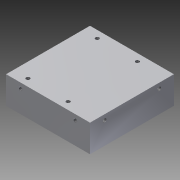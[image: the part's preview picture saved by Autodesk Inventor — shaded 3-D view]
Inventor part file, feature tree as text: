
AUTODESK INVENTOR PART (.ipt)
format: ipt  version: 2013 (Build 170138000, 138)  size: 140,288 bytes
history: native  units: mm
features: thread x12, sketch x4, hole x3, other x1, extrude x1
ambient origin geometry x1: Origin
feature tree (21):
  other  "ソリッド1"
  extrude  "押し出し1"  Depth=46.0mm
  hole  "穴1"  [1 undecoded]
  hole  "穴2"  [1 undecoded]
  hole  "穴3"  [1 undecoded]
  thread  "ねじ1"
  thread  "ねじ3"
  thread  "ねじ5"
  thread  "ねじ6"
  thread  "ねじ11"
  thread  "ねじ13"
  thread  "ねじ14"
  thread  "ねじ16"
  thread  "ねじ17"
  thread  "ねじ18"
  thread  "ねじ19"
  thread  "ねじ20"
  sketch  "スケッチ1"
  sketch  "スケッチ2"
  sketch  "スケッチ3"
  sketch  "スケッチ4"
note: 3 required parameter values undecoded (feature->parameter linkage not recoverable at this tier; creation-order binding heuristic only, values carry confidence <= 0.55)
